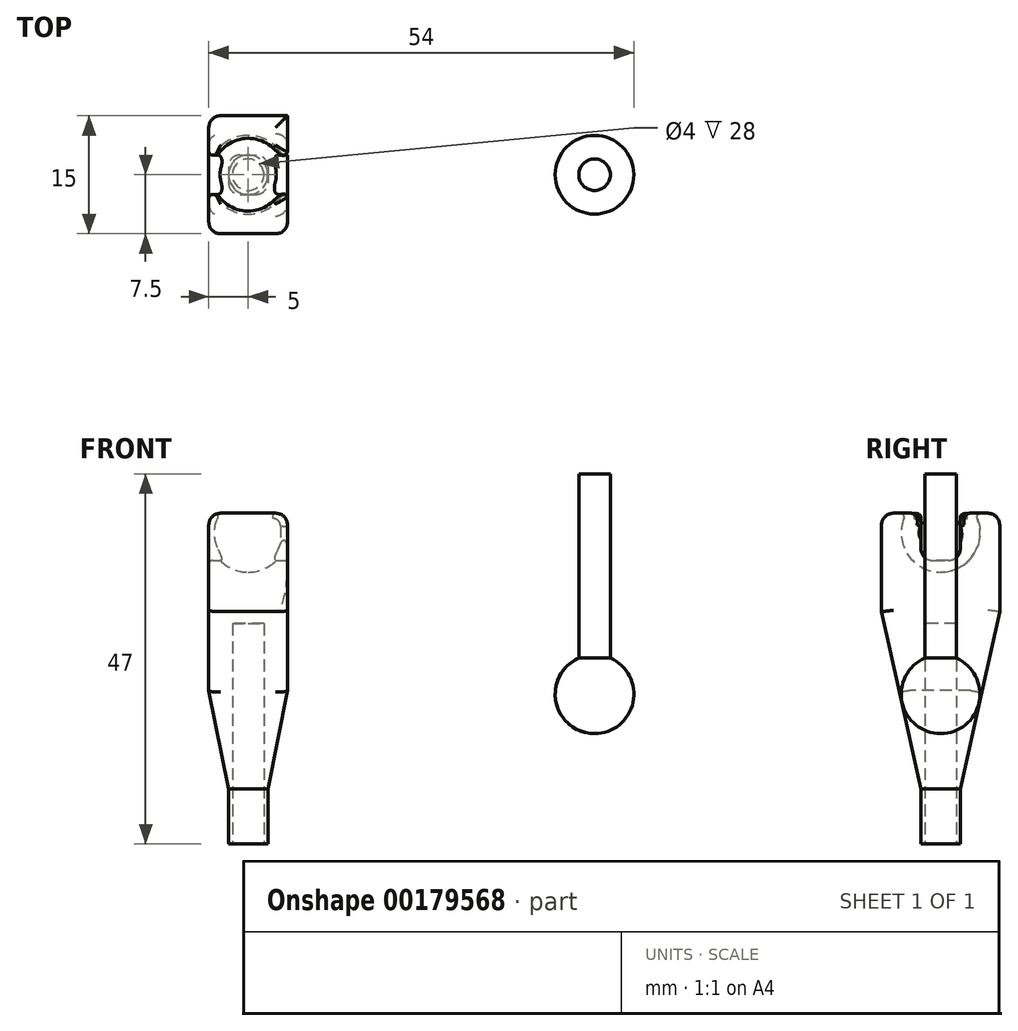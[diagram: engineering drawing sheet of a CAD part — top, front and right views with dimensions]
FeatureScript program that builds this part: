
annotation { "Feature Type Name" : "Feature", "Feature Type Description" : "" }
export const myFeature = defineFeature(function(context is Context, id is Id, definition is map)
    precondition{}
    {
        {
            var Q0;
            Q0=qCreatedBy(makeId("Right.planeOp"),FACE);
            var sketch = newSketch(context, id + "F0", { "sketchPlane" : qUnion([Q0])});
            skLineSegment(sketch, "E0.bottom", {"start": v(-7.5, 50.25) * mm, "end": v(7.5, 50.25) * mm});
            skLineSegment(sketch, "E0.top", {"start": v(-7.5, 15.25) * mm, "end": v(7.5, 15.25) * mm});
            skLineSegment(sketch, "E0.left", {"start": v(-7.5, 50.25) * mm, "end": v(-7.5, 15.25) * mm});
            skLineSegment(sketch, "E0.right", {"start": v(7.5, 50.25) * mm, "end": v(7.5, 15.25) * mm});
            skSolve(sketch);
        }
        {
            var Q0;
            Q0=qSketchRegion(id+"F0",true);
            extrude(context, id + "F1", {"entities" : qUnion([Q0]), "endBound" : BoundingType.SYMMETRIC, "depth" : 10 * mm});
        }
        {
            var Q0;
            Q0=makeQuery(id+"F1.opExtrude","CAP_FACE",FACE,{"disambiguationData":[OSD([sQuery(id+"F0.wireOp",EDGE,"E0.bottom"),sQuery(id+"F0.wireOp",EDGE,"E0.top"),sQuery(id+"F0.wireOp",EDGE,"E0.left"),sQuery(id+"F0.wireOp",EDGE,"E0.right")])],"isStart":false});
            var sketch = newSketch(context, id + "F2", { "sketchPlane" : qUnion([Q0])});
            skLineSegment(sketch, "E1", {"start": v(-7.5, 15.25) * mm, "end": v(-7.5, 37.75) * mm});
            skLineSegment(sketch, "E2", {"start": v(-7.5, 37.75) * mm, "end": v(-2.5, 15.25) * mm});
            skLineSegment(sketch, "E3", {"start": v(-2.5, 15.25) * mm, "end": v(-7.5, 15.25) * mm});
            skLineSegment(sketch, "E4", {"start": v(0, 50.25) * mm, "end": v(0, 15.25) * mm, "construction": true});
            skLineSegment(sketch, "E5.MirrorCS", {"start": v(7.5, 15.25) * mm, "end": v(7.5, 37.75) * mm});
            skLineSegment(sketch, "E6.MirrorCS", {"start": v(7.5, 37.75) * mm, "end": v(2.5, 15.25) * mm});
            skLineSegment(sketch, "E7.MirrorCS", {"start": v(2.5, 15.25) * mm, "end": v(7.5, 15.25) * mm});
            skSolve(sketch);
        }
        {
            var Q0;
            Q0=qSketchRegion(id+"F2",true);
            extrude(context, id + "F3", {"entities" : qUnion([Q0]), "operationType" : NewBodyOperationType.REMOVE, "endBound" : BoundingType.SYMMETRIC, "oppositeDirection" : true, "depth" : 25 * mm});
        }
        {
            var Q0;
            Q0=qCreatedBy(makeId("Front.planeOp"),FACE);
            var sketch = newSketch(context, id + "F4", { "sketchPlane" : qUnion([Q0])});
            skLineSegment(sketch, "E8", {"start": v(5, 27.75) * mm, "end": v(5, 15.25) * mm});
            skLineSegment(sketch, "E9", {"start": v(5, 15.25) * mm, "end": v(2.5, 15.25) * mm});
            skLineSegment(sketch, "E10", {"start": v(2.5, 15.25) * mm, "end": v(5, 27.75) * mm});
            skLineSegment(sketch, "E11", {"start": v(0, 10.16) * mm, "end": v(0, 28) * mm, "construction": true});
            skLineSegment(sketch, "E12.MirrorCS", {"start": v(-5, 27.75) * mm, "end": v(-5, 15.25) * mm});
            skLineSegment(sketch, "E13.MirrorCS", {"start": v(-5, 15.25) * mm, "end": v(-2.5, 15.25) * mm});
            skLineSegment(sketch, "E14.MirrorCS", {"start": v(-2.5, 15.25) * mm, "end": v(-5, 27.75) * mm});
            skSolve(sketch);
        }
        {
            var Q0;
            Q0=qSketchRegion(id+"F4",true);
            extrude(context, id + "F5", {"entities" : qUnion([Q0]), "operationType" : NewBodyOperationType.REMOVE, "endBound" : BoundingType.SYMMETRIC, "oppositeDirection" : true, "depth" : 50 * mm});
        }
        {
            var Q0;
            Q0=makeQuery(id+"F3.boolean.opBoolean","INTERSECT",EDGE,{"derivedFrom":[makeQuery(id+"F1.opExtrude","CAP_FACE",FACE,{"disambiguationData":[OSD([sQuery(id+"F0.wireOp",EDGE,"E0.bottom"),sQuery(id+"F0.wireOp",EDGE,"E0.top"),sQuery(id+"F0.wireOp",EDGE,"E0.left"),sQuery(id+"F0.wireOp",EDGE,"E0.right")])],"isStart":true}),makeQuery(id+"F3.opExtrude","SWEPT_FACE",FACE,{"disambiguationData":[OSD([sQuery(id+"F2.wireOp",EDGE,"E2")])]})]});
            var Q1;
            Q1=makeQuery(id+"F5.boolean.opBoolean","INTERSECT",EDGE,{"derivedFrom":[makeQuery(id+"F3.boolean.opBoolean","COPY",FACE,{"derivedFrom":makeQuery(id+"F3.opExtrude","SWEPT_FACE",FACE,{"disambiguationData":[OSD([sQuery(id+"F2.wireOp",EDGE,"E2")])]})}),makeQuery(id+"F5.opExtrude","SWEPT_FACE",FACE,{"disambiguationData":[OSD([sQuery(id+"F4.wireOp",EDGE,"E14.MirrorCS")])]})]});
            var Q2;
            Q2=makeQuery(id+"F5.boolean.opBoolean","INTERSECT",EDGE,{"derivedFrom":[makeQuery(id+"F3.boolean.opBoolean","COPY",FACE,{"derivedFrom":makeQuery(id+"F3.opExtrude","SWEPT_FACE",FACE,{"disambiguationData":[OSD([sQuery(id+"F2.wireOp",EDGE,"E2")])]})}),makeQuery(id+"F5.opExtrude","SWEPT_FACE",FACE,{"disambiguationData":[OSD([sQuery(id+"F4.wireOp",EDGE,"E10")])]})]});
            var Q3;
            Q3=makeQuery(id+"F3.boolean.opBoolean","INTERSECT",EDGE,{"derivedFrom":[makeQuery(id+"F1.opExtrude","CAP_FACE",FACE,{"disambiguationData":[OSD([sQuery(id+"F0.wireOp",EDGE,"E0.bottom"),sQuery(id+"F0.wireOp",EDGE,"E0.top"),sQuery(id+"F0.wireOp",EDGE,"E0.left"),sQuery(id+"F0.wireOp",EDGE,"E0.right")])],"isStart":false}),makeQuery(id+"F3.opExtrude","SWEPT_FACE",FACE,{"disambiguationData":[OSD([sQuery(id+"F2.wireOp",EDGE,"E2")])]})]});
            var Q4;
            Q4=makeQuery(id+"F1.opExtrude","CAP_EDGE",EDGE,{"disambiguationData":[OSD([sQuery(id+"F0.wireOp",EDGE,"E0.left")])],"isStart":false});
            var Q5;
            Q5=makeQuery(id+"F1.opExtrude","CAP_EDGE",EDGE,{"disambiguationData":[OSD([sQuery(id+"F0.wireOp",EDGE,"E0.left")])],"isStart":true});
            var Q6;
            Q6=makeQuery(id+"F1.opExtrude","CAP_EDGE",EDGE,{"disambiguationData":[OSD([sQuery(id+"F0.wireOp",EDGE,"E0.right")])],"isStart":true});
            var Q7;
            Q7=makeQuery(id+"F3.boolean.opBoolean","INTERSECT",EDGE,{"derivedFrom":[makeQuery(id+"F1.opExtrude","CAP_FACE",FACE,{"disambiguationData":[OSD([sQuery(id+"F0.wireOp",EDGE,"E0.bottom"),sQuery(id+"F0.wireOp",EDGE,"E0.top"),sQuery(id+"F0.wireOp",EDGE,"E0.left"),sQuery(id+"F0.wireOp",EDGE,"E0.right")])],"isStart":true}),makeQuery(id+"F3.opExtrude","SWEPT_FACE",FACE,{"disambiguationData":[OSD([sQuery(id+"F2.wireOp",EDGE,"E6.MirrorCS")])]})]});
            var Q8;
            Q8=makeQuery(id+"F5.boolean.opBoolean","INTERSECT",EDGE,{"derivedFrom":[makeQuery(id+"F3.boolean.opBoolean","COPY",FACE,{"derivedFrom":makeQuery(id+"F3.opExtrude","SWEPT_FACE",FACE,{"disambiguationData":[OSD([sQuery(id+"F2.wireOp",EDGE,"E6.MirrorCS")])]})}),makeQuery(id+"F5.opExtrude","SWEPT_FACE",FACE,{"disambiguationData":[OSD([sQuery(id+"F4.wireOp",EDGE,"E14.MirrorCS")])]})]});
            var Q9;
            Q9=makeQuery(id+"F5.boolean.opBoolean","INTERSECT",EDGE,{"derivedFrom":[makeQuery(id+"F3.boolean.opBoolean","COPY",FACE,{"derivedFrom":makeQuery(id+"F3.opExtrude","SWEPT_FACE",FACE,{"disambiguationData":[OSD([sQuery(id+"F2.wireOp",EDGE,"E6.MirrorCS")])]})}),makeQuery(id+"F5.opExtrude","SWEPT_FACE",FACE,{"disambiguationData":[OSD([sQuery(id+"F4.wireOp",EDGE,"E10")])]})]});
            var Q10;
            Q10=makeQuery(id+"F3.boolean.opBoolean","INTERSECT",EDGE,{"derivedFrom":[makeQuery(id+"F1.opExtrude","CAP_FACE",FACE,{"disambiguationData":[OSD([sQuery(id+"F0.wireOp",EDGE,"E0.bottom"),sQuery(id+"F0.wireOp",EDGE,"E0.top"),sQuery(id+"F0.wireOp",EDGE,"E0.left"),sQuery(id+"F0.wireOp",EDGE,"E0.right")])],"isStart":false}),makeQuery(id+"F3.opExtrude","SWEPT_FACE",FACE,{"disambiguationData":[OSD([sQuery(id+"F2.wireOp",EDGE,"E6.MirrorCS")])]})]});
            var Q11;
            Q11=makeQuery(id+"F3.boolean.opBoolean","COPY",EDGE,{"derivedFrom":makeQuery(id+"F3.opExtrude","SWEPT_EDGE",EDGE,{"disambiguationData":[OSD([sQuery(id+"F0.wireOp",EDGE,"E0.right"),sQuery(id+"F2.wireOp",EDGE,"E5.MirrorCS"),sQuery(id+"F2.wireOp",EDGE,"E6.MirrorCS")])]})});
            var Q12;
            Q12=makeQuery(id+"F3.boolean.opBoolean","COPY",EDGE,{"derivedFrom":makeQuery(id+"F3.opExtrude","SWEPT_EDGE",EDGE,{"disambiguationData":[OSD([sQuery(id+"F0.wireOp",EDGE,"E0.left"),sQuery(id+"F2.wireOp",EDGE,"E1"),sQuery(id+"F2.wireOp",EDGE,"E2")])]})});
            var Q13;
            Q13=makeQuery(id+"F1.opExtrude","SWEPT_EDGE",EDGE,{"disambiguationData":[OSD([sQuery(id+"F0.wireOp",EDGE,"E0.bottom"),sQuery(id+"F0.wireOp",EDGE,"E0.left")])]});
            var Q14;
            Q14=makeQuery(id+"F1.opExtrude","CAP_EDGE",EDGE,{"disambiguationData":[OSD([sQuery(id+"F0.wireOp",EDGE,"E0.bottom")])],"isStart":true});
            var Q15;
            Q15=makeQuery(id+"F1.opExtrude","CAP_EDGE",EDGE,{"disambiguationData":[OSD([sQuery(id+"F0.wireOp",EDGE,"E0.bottom")])],"isStart":false});
            var Q16;
            Q16=makeQuery(id+"F1.opExtrude","SWEPT_EDGE",EDGE,{"disambiguationData":[OSD([sQuery(id+"F0.wireOp",EDGE,"E0.bottom"),sQuery(id+"F0.wireOp",EDGE,"E0.right")])]});
            fillet(context, id + "F6", {"entities" : qUnion([Q0, Q1, Q2, Q3, Q4, Q5, Q6, Q7, Q8, Q9, Q10, Q11, Q12, Q13, Q14, Q15, Q16]), "radius" : 1.5 * mm, "tangentPropagation" : true, "allowEdgeOverflow" : false});
        }
        {
            var Q0;
            Q0=makeQuery(id+"F1.opExtrude","SWEPT_FACE",FACE,{"disambiguationData":[OSD([sQuery(id+"F0.wireOp",EDGE,"E0.top")])]});
            var sketch = newSketch(context, id + "F7", { "sketchPlane" : qUnion([Q0])});
            skPoint(sketch, "E15.cCircle.perimeterSnap0", {"position": v(2.5, 0) * mm});
            skPoint(sketch, "E15.cCircle.perimeterSnap1", {"position": v(2.09, 0.04) * mm});
            skPoint(sketch, "E15.0.midPoint", {"position": v(2.09, 0) * mm});
            skPoint(sketch, "E15.0.midPoint.positionSnap0", {"position": v(2.5, 0) * mm});
            skPoint(sketch, "E15.0.midPoint.positionSnap1", {"position": v(2.09, 0.04) * mm});
            skCircle(sketch, "E16", {"center": v(0, 0) * mm, "radius": 2.5 * mm});
            skSolve(sketch);
        }
        {
            var Q0;
            Q0=qSketchRegion(id+"F7",true);
            extrude(context, id + "F8", {"entities" : qUnion([Q0]), "operationType" : NewBodyOperationType.ADD, "depth" : 7 * mm});
        }
        {
            var Q0;
            Q0=makeQuery(id+"F1.opExtrude","CAP_FACE",FACE,{"disambiguationData":[OSD([sQuery(id+"F0.wireOp",EDGE,"E0.bottom"),sQuery(id+"F0.wireOp",EDGE,"E0.top"),sQuery(id+"F0.wireOp",EDGE,"E0.left"),sQuery(id+"F0.wireOp",EDGE,"E0.right")])],"isStart":false});
            var sketch = newSketch(context, id + "F9", { "sketchPlane" : qUnion([Q0])});
            skLineSegment(sketch, "E17.bottom", {"start": v(-2.5, 50.25) * mm, "end": v(2.5, 50.25) * mm});
            skLineSegment(sketch, "E17.top", {"start": v(-1, 44.25) * mm, "end": v(1, 44.25) * mm});
            skLineSegment(sketch, "E17.left", {"start": v(-2.5, 50.25) * mm, "end": v(-2.5, 45.75) * mm});
            skLineSegment(sketch, "E17.right", {"start": v(2.5, 50.25) * mm, "end": v(2.5, 45.75) * mm});
            skPoint(sketch, "E18.visualSharp", {"position": v(-2.5, 44.25) * mm});
            skArc(sketch, "E18.filletArc", {"start": v(-2.5, 45.75) * mm, "mid": v(-2.06, 44.69) * mm, "end": v(-1, 44.25) * mm});
            skPoint(sketch, "E19.visualSharp", {"position": v(2.5, 44.25) * mm});
            skArc(sketch, "E19.filletArc", {"start": v(1, 44.25) * mm, "mid": v(2.06, 44.69) * mm, "end": v(2.5, 45.75) * mm});
            skSolve(sketch);
        }
        {
            var Q0;
            Q0=qSketchRegion(id+"F9",true);
            extrude(context, id + "F10", {"entities" : qUnion([Q0]), "operationType" : NewBodyOperationType.REMOVE, "endBound" : BoundingType.THROUGH_ALL, "oppositeDirection" : true, "depth" : 25 * mm});
        }
        {
            var Q0;
            Q0=qCreatedBy(makeId("Right.planeOp"),FACE);
            var sketch = newSketch(context, id + "F11", { "sketchPlane" : qUnion([Q0])});
            skLineSegment(sketch, "E20", {"start": v(0, 52.75) * mm, "end": v(0, 42.75) * mm});
            skLineSegment(sketch, "E21", {"start": v(0, 54.58) * mm, "end": v(0, 40) * mm, "construction": true});
            skPoint(sketch, "E22.center.orphan", {"position": v(0, 47.75) * mm});
            skArc(sketch, "E23", {"start": v(0, 52.75) * mm, "mid": v(-5, 47.75) * mm, "end": v(0, 42.75) * mm});
            skSolve(sketch);
        }
        {
            var Q0;
            Q0=qSketchRegion(id+"F11",true);
            var Q1;
            Q1=sQuery(id+"F11.wireOp",EDGE,"E21");
            revolve(context, id + "F12", {"operationType" : NewBodyOperationType.REMOVE, "entities" : qUnion([Q0]), "axis" : qUnion([Q1]), "revolveType" : RevolveType.FULL, "oppositeDirection" : true});
        }
        {
            var Q0;
            Q0=makeQuery(id+"F10.boolean.opBoolean","COPY",EDGE,{"derivedFrom":makeQuery(id+"F10.opExtrude","CAP_EDGE",EDGE,{"disambiguationData":[OSD([sQuery(id+"F9.wireOp",EDGE,"E17.left")])],"isStart":true})});
            var Q1;
            {var subQ0=sQuery(id+"F0.wireOp",EDGE,"E0.bottom");Q1=makeQuery(id+"F12.boolean.opBoolean","INTERSECT",EDGE,{"derivedFrom":[makeQuery(id+"F10.boolean.opBoolean","SPLIT",FACE,{"disambiguationData":[TD([makeQuery(id+"F10.opExtrude","SWEPT_FACE",FACE,{"disambiguationData":[OSD([sQuery(id+"F9.wireOp",EDGE,"E17.right")])]})])],"derivedFrom":makeQuery(id+"F1.opExtrude","SWEPT_FACE",FACE,{"disambiguationData":[OSD([subQ0])]})}),makeQuery(id+"F12.opRevolve","SWEPT_FACE",FACE,{"disambiguationData":[OSD([sQuery(id+"F11.wireOp",EDGE,"E23")])]})]});}
            var Q2;
            {var subQ0=sQuery(id+"F0.wireOp",EDGE,"E0.bottom");Q2=makeQuery(id+"F12.boolean.opBoolean","INTERSECT",EDGE,{"derivedFrom":[makeQuery(id+"F10.boolean.opBoolean","SPLIT",FACE,{"disambiguationData":[TD([makeQuery(id+"F10.opExtrude","SWEPT_FACE",FACE,{"disambiguationData":[OSD([sQuery(id+"F9.wireOp",EDGE,"E17.left")])]})])],"derivedFrom":makeQuery(id+"F1.opExtrude","SWEPT_FACE",FACE,{"disambiguationData":[OSD([subQ0])]})}),makeQuery(id+"F12.opRevolve","SWEPT_FACE",FACE,{"disambiguationData":[OSD([sQuery(id+"F11.wireOp",EDGE,"E23")])]})]});}
            var Q3;
            Q3=makeQuery(id+"F10.boolean.opBoolean","INTERSECT",EDGE,{"derivedFrom":[makeQuery(id+"F1.opExtrude","CAP_FACE",FACE,{"disambiguationData":[OSD([sQuery(id+"F0.wireOp",EDGE,"E0.bottom"),sQuery(id+"F0.wireOp",EDGE,"E0.top"),sQuery(id+"F0.wireOp",EDGE,"E0.left"),sQuery(id+"F0.wireOp",EDGE,"E0.right")])],"isStart":true}),makeQuery(id+"F10.opExtrude","SWEPT_FACE",FACE,{"disambiguationData":[OSD([sQuery(id+"F9.wireOp",EDGE,"E18.filletArc")])]})]});
            fillet(context, id + "F13", {"entities" : qUnion([Q0, Q1, Q2, Q3]), "radius" : 0.5 * mm, "tangentPropagation" : true, "allowEdgeOverflow" : false});
        }
        {
            var Q0;
            Q0=makeQuery(id+"F8.opExtrude","CAP_FACE",FACE,{"disambiguationData":[OSD([sQuery(id+"F7.wireOp",EDGE,"E16")])],"isStart":false});
            var sketch = newSketch(context, id + "F14", { "sketchPlane" : qUnion([Q0])});
            skCircle(sketch, "E24", {"center": v(0, 0) * mm, "radius": 2 * mm});
            skSolve(sketch);
        }
        {
            var Q0;
            Q0=makeQuery(id+"F14.imprint","IMPRINT",FACE,{"disambiguationData":[TD([[makeQuery(id+"F14.imprint","IMPRINT",EDGE,{"derivedFrom":sQuery(id+"F14.wireOp",EDGE,"E24")}),1.0]])]});
            extrude(context, id + "F15", {"entities" : qUnion([Q0]), "operationType" : NewBodyOperationType.REMOVE, "oppositeDirection" : true, "depth" : 28 * mm});
        }
        {
            var Q0;
            Q0=qCreatedBy(makeId("Front.planeOp"),FACE);
            var sketch = newSketch(context, id + "F16", { "sketchPlane" : qUnion([Q0])});
            skLineSegment(sketch, "E25.bottom", {"start": v(44, 55.25) * mm, "end": v(46, 55.25) * mm});
            skLineSegment(sketch, "E25.left", {"start": v(44, 55.25) * mm, "end": v(44, 27.25) * mm});
            skLineSegment(sketch, "E25.right", {"start": v(46, 55.25) * mm, "end": v(46, 31.84) * mm});
            skArc(sketch, "E26", {"start": v(44, 22.25) * mm, "mid": v(48.9, 26.23) * mm, "end": v(46, 31.84) * mm});
            skLineSegment(sketch, "E27", {"start": v(44, 27.25) * mm, "end": v(44, 22.25) * mm});
            skLineSegment(sketch, "E28", {"start": v(44, 18.57) * mm, "end": v(44, 60.46) * mm, "construction": true});
            skSolve(sketch);
        }
        {
            var Q0;
            Q0 = qSketchRegion(id + "F16", true);
            var Q1;
            Q1=sQuery(id+"F16.wireOp",EDGE,"E28");
            revolve(context, id + "F17", {"entities" : qUnion([Q0]), "axis" : qUnion([Q1]), "revolveType" : RevolveType.FULL});
        }
    });
